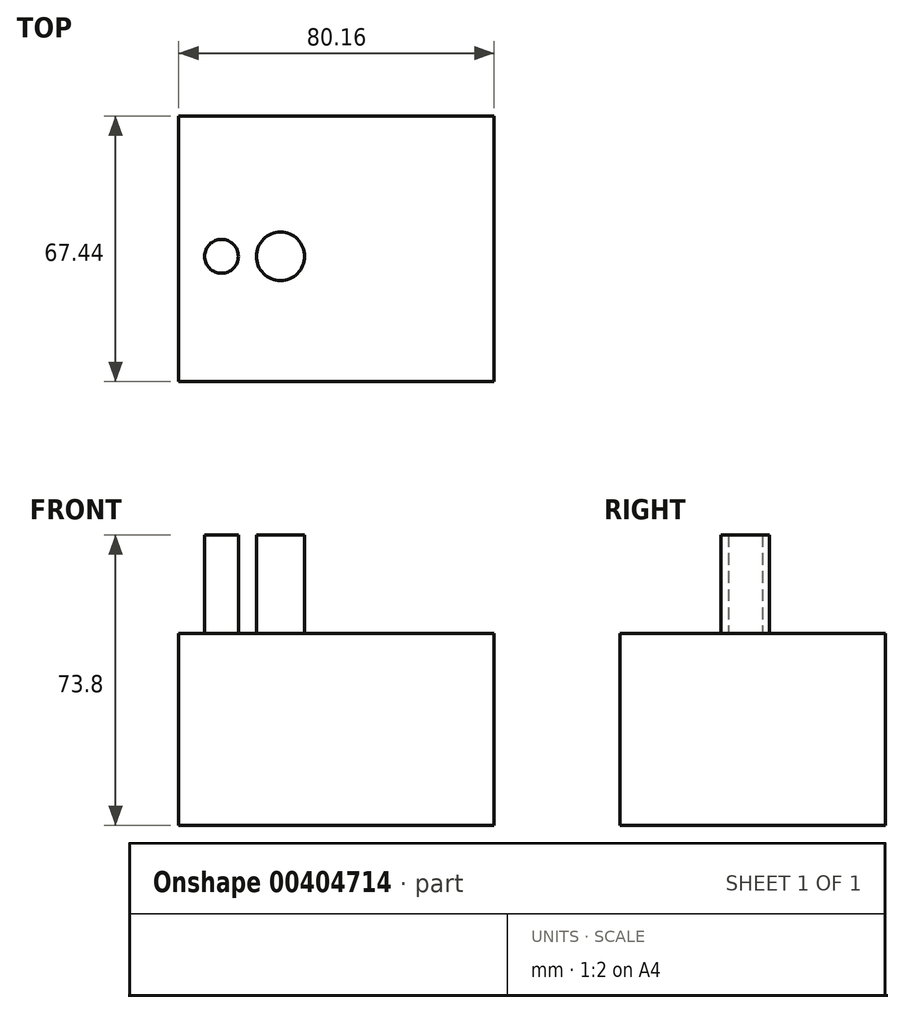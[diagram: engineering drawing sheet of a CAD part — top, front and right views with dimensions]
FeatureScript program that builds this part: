
annotation { "Feature Type Name" : "Feature", "Feature Type Description" : "" }
export const myFeature = defineFeature(function(context is Context, id is Id, definition is map)
    precondition{}
    {
        {
            var Q0;
            Q0=qCreatedBy(makeId("Top.planeOp"),FACE);
            var sketch = newSketch(context, id + "F0", { "sketchPlane" : qUnion([Q0])});
            skLineSegment(sketch, "E0.bottom", {"start": v(-37.86, 35.64) * mm, "end": v(42.3, 35.64) * mm});
            skLineSegment(sketch, "E0.top", {"start": v(-37.86, -31.8) * mm, "end": v(42.3, -31.8) * mm});
            skLineSegment(sketch, "E0.left", {"start": v(-37.86, 35.64) * mm, "end": v(-37.86, -31.8) * mm});
            skLineSegment(sketch, "E0.right", {"start": v(42.3, 35.64) * mm, "end": v(42.3, -31.8) * mm});
            skSolve(sketch);
        }
        {
            var Q0;
            Q0=makeQuery(id+"F0.imprint","IMPRINT",FACE,{"disambiguationData":[TD([[makeQuery(id+"F0.imprint","IMPRINT",EDGE,{"derivedFrom":sQuery(id+"F0.wireOp",EDGE,"E0.bottom")}),-1.0]])]});
            extrude(context, id + "F1", {"entities" : qUnion([Q0]), "depth" : 48.8 * mm});
        }
        {
            var Q0;
            Q0=makeQuery(id+"F1.opExtrude","CAP_FACE",FACE,{"disambiguationData":[OSD([sQuery(id+"F0.wireOp",EDGE,"E0.bottom"),sQuery(id+"F0.wireOp",EDGE,"E0.top"),sQuery(id+"F0.wireOp",EDGE,"E0.left"),sQuery(id+"F0.wireOp",EDGE,"E0.right")])],"isStart":false});
            var sketch = newSketch(context, id + "F2", { "sketchPlane" : qUnion([Q0])});
            skLineSegment(sketch, "E1.bottom", {"start": v(-29.18, -23.95) * mm, "end": v(35.8, -23.95) * mm});
            skLineSegment(sketch, "E1.top", {"start": v(-29.18, 31.56) * mm, "end": v(35.8, 31.56) * mm});
            skLineSegment(sketch, "E1.left", {"start": v(-29.18, -23.95) * mm, "end": v(-29.18, 31.56) * mm});
            skLineSegment(sketch, "E1.right", {"start": v(35.8, -23.95) * mm, "end": v(35.8, 31.56) * mm});
            skSolve(sketch);
        }
        {
            var Q0;
            Q0=makeQuery(id+"F2.imprint","IMPRINT",FACE,{"disambiguationData":[TD([[makeQuery(id+"F2.imprint","IMPRINT",EDGE,{"derivedFrom":sQuery(id+"F2.wireOp",EDGE,"E1.bottom")}),1.0]])]});
            extrude(context, id + "F3", {"entities" : qUnion([Q0]), "operationType" : NewBodyOperationType.ADD, "depth" : -20 * mm});
        }
        {
            var Q0;
            Q0=makeQuery(id+"F1.opExtrude","CAP_FACE",FACE,{"disambiguationData":[OSD([sQuery(id+"F0.wireOp",EDGE,"E0.bottom"),sQuery(id+"F0.wireOp",EDGE,"E0.top"),sQuery(id+"F0.wireOp",EDGE,"E0.left"),sQuery(id+"F0.wireOp",EDGE,"E0.right")])],"isStart":false});
            var sketch = newSketch(context, id + "F4", { "sketchPlane" : qUnion([Q0])});
            skCircle(sketch, "E2", {"center": v(-26.98, 0) * mm, "radius": 4.3 * mm});
            skSolve(sketch);
        }
        {
            var Q0;
            Q0 = qSketchRegion(id + "F4", true);
            extrude(context, id + "F5", {"entities" : qUnion([Q0]), "operationType" : NewBodyOperationType.ADD, "depth" : 25 * mm});
        }
        {
            var Q0;
            Q0=makeQuery(id+"F1.opExtrude","CAP_FACE",FACE,{"disambiguationData":[OSD([sQuery(id+"F0.wireOp",EDGE,"E0.bottom"),sQuery(id+"F0.wireOp",EDGE,"E0.top"),sQuery(id+"F0.wireOp",EDGE,"E0.left"),sQuery(id+"F0.wireOp",EDGE,"E0.right")])],"isStart":false});
            var sketch = newSketch(context, id + "F6", { "sketchPlane" : qUnion([Q0])});
            skCircle(sketch, "E3", {"center": v(-11.98, 0) * mm, "radius": 6.14 * mm});
            skSolve(sketch);
        }
        {
            var Q0;
            Q0=makeQuery(id+"F6.imprint","IMPRINT",FACE,{"disambiguationData":[TD([[makeQuery(id+"F6.imprint","IMPRINT",EDGE,{"derivedFrom":sQuery(id+"F6.wireOp",EDGE,"E3")}),1.0]])]});
            extrude(context, id + "F7", {"entities" : qUnion([Q0]), "operationType" : NewBodyOperationType.ADD, "depth" : 25 * mm});
        }
    });
